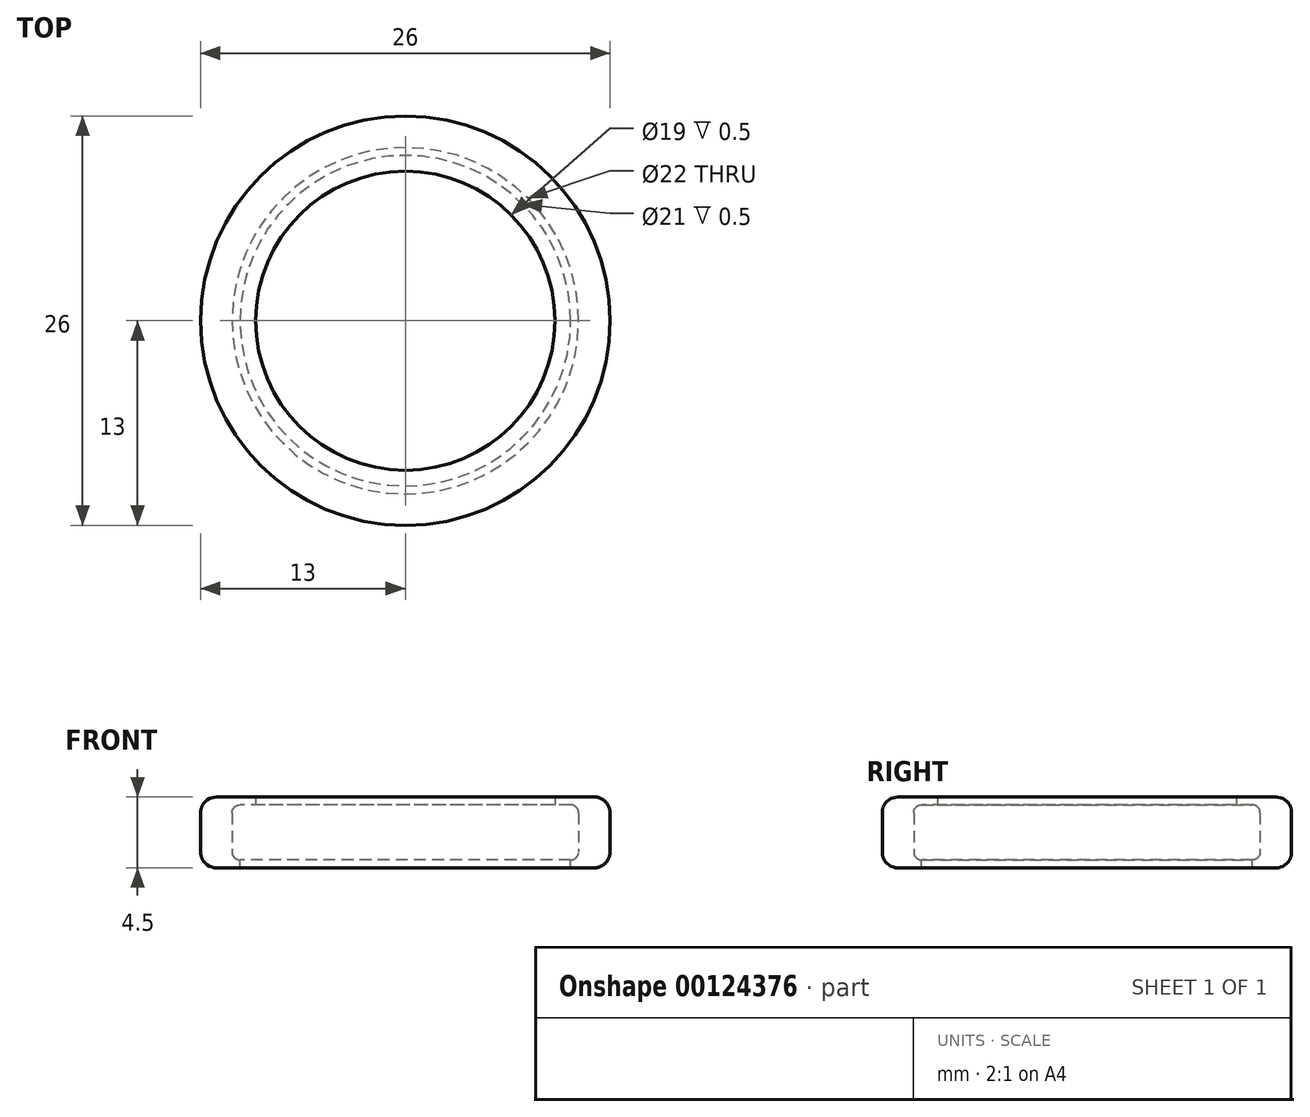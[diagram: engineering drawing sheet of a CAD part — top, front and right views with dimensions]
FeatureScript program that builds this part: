
annotation { "Feature Type Name" : "Feature", "Feature Type Description" : "" }
export const myFeature = defineFeature(function(context is Context, id is Id, definition is map)
    precondition{}
    {
        {
            var Q0;
            Q0=qCreatedBy(makeId("Top.planeOp"),FACE);
            var sketch = newSketch(context, id + "F0", { "sketchPlane" : qUnion([Q0])});
            skCircle(sketch, "E0", {"center": v(0, 0) * mm, "radius": 11 * mm});
            skCircle(sketch, "E1", {"center": v(0, 0) * mm, "radius": 4 * mm});
            skSolve(sketch);
        }
        {
            var Q0;
            Q0=makeQuery(id+"F0.imprint","IMPRINT",FACE,{"disambiguationData":[TD([[makeQuery(id+"F0.imprint","IMPRINT",EDGE,{"derivedFrom":sQuery(id+"F0.wireOp",EDGE,"E0")}),1.0]])]});
            extrude(context, id + "F1", {"entities" : qUnion([Q0]), "endBound" : BoundingType.SYMMETRIC, "depth" : 3.5 * mm});
        }
        {
            var Q0;
            Q0=qCreatedBy(makeId("Top.planeOp"),FACE);
            var sketch = newSketch(context, id + "F2", { "sketchPlane" : qUnion([Q0])});
            skCircle(sketch, "E2", {"center": v(0, 0) * mm, "radius": 13 * mm});
            skCircle(sketch, "E3", {"center": v(0, 0) * mm, "radius": 9.5 * mm});
            skCircle(sketch, "E4", {"center": v(0, 0) * mm, "radius": 10.5 * mm});
            skSolve(sketch);
        }
        {
            var Q0;
            Q0=makeQuery(id+"F2.imprint","IMPRINT",FACE,{"disambiguationData":[TD([[makeQuery(id+"F2.imprint","IMPRINT",EDGE,{"derivedFrom":sQuery(id+"F2.wireOp",EDGE,"E2")}),1.0]])]});
            var Q1;
            Q1=makeQuery(id+"F2.imprint","IMPRINT",FACE,{"disambiguationData":[TD([[makeQuery(id+"F2.imprint","IMPRINT",EDGE,{"derivedFrom":sQuery(id+"F2.wireOp",EDGE,"E3")}),-1.0]])]});
            extrude(context, id + "F3", {"entities" : qUnion([Q0, Q1]), "endBound" : BoundingType.SYMMETRIC, "depth" : 4.5 * mm});
        }
        {
            var Q0;
            Q0=makeQuery(id+"F3.opExtrude","CAP_EDGE",EDGE,{"disambiguationData":[OSD([sQuery(id+"F2.wireOp",EDGE,"E2")])],"isStart":false});
            var Q1;
            Q1=makeQuery(id+"F3.opExtrude","CAP_EDGE",EDGE,{"disambiguationData":[OSD([sQuery(id+"F2.wireOp",EDGE,"E2")])],"isStart":true});
            fillet(context, id + "F4", {"entities" : qUnion([Q0, Q1]), "radius" : 1 * mm, "tangentPropagation" : true, "allowEdgeOverflow" : false});
        }
        {
            var Q0;
            Q0=makeQuery(id+"F0.imprint","IMPRINT",FACE,{"disambiguationData":[TD([[makeQuery(id+"F0.imprint","IMPRINT",EDGE,{"derivedFrom":sQuery(id+"F0.wireOp",EDGE,"E0")}),1.0]])]});
            extrude(context, id + "F5", {"entities" : qUnion([Q0]), "operationType" : NewBodyOperationType.REMOVE, "endBound" : BoundingType.SYMMETRIC, "depth" : 3.5 * mm});
        }
        {
            var Q0;
            Q0=makeQuery(id+"F5.boolean.opBoolean","COPY",EDGE,{"derivedFrom":makeQuery(id+"F5.opExtrude","CAP_EDGE",EDGE,{"disambiguationData":[OSD([sQuery(id+"F0.wireOp",EDGE,"E0")])],"isStart":true})});
            var Q1;
            Q1=makeQuery(id+"F5.boolean.opBoolean","COPY",EDGE,{"derivedFrom":makeQuery(id+"F5.opExtrude","CAP_EDGE",EDGE,{"disambiguationData":[OSD([sQuery(id+"F0.wireOp",EDGE,"E0")])],"isStart":false})});
            fillet(context, id + "F6", {"entities" : qUnion([Q0, Q1]), "radius" : .5 * mm, "tangentPropagation" : true, "allowEdgeOverflow" : false});
        }
        {
            var Q0;
            Q0=makeQuery(id+"F2.imprint","IMPRINT",FACE,{"disambiguationData":[TD([[makeQuery(id+"F2.imprint","IMPRINT",EDGE,{"derivedFrom":sQuery(id+"F2.wireOp",EDGE,"E3")}),-1.0]])]});
            extrude(context, id + "F7", {"entities" : qUnion([Q0]), "operationType" : NewBodyOperationType.REMOVE, "oppositeDirection" : true, "depth" : 25 * mm});
        }
    });
